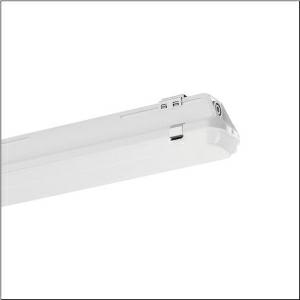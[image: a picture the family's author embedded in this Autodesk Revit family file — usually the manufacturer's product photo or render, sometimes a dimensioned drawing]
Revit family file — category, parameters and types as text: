
# Revit family: monsun_r__12_facade_51ff40mp460h_f970
name_source: partatom
category: Lighting Fixtures
units: mm (PartAtom-declared; Revit-internal decimal feet)

## family parameters
Cut with Voids When Loaded = No
Host = Face
Light Source = No
Part Type = Normal
Room Calculation Point = No
Round Connector Dimension = Use Diameter
Shared = No

## types (1)
- --- (1 x LED, 6110 lm, 33.5 W, 4000K)
    Apparent Load = 34 VA
    CIE Flux Codes = 47 77 93 95 100
    Color Rendering = 80
    Color Temperature = 4000K
    Default Elevation = 1800 mm
    Description = Monsun® 12 facade, damp-proof luminaire, chain hanger, primary optical cover: enclosure, of PMMA, light emission: direct distribution, primary light characteristic: symmetric, installation type: surface-mounted, horizontal mounting, vertical mounting, LED rated luminous flux: 6.110 lm, light colour: 840, colour temperature: 4000K, control gear: ECG, with terminal, 3-pole, max. 2.5mm², mains connection: 220..240V, AC, 50/60Hz, rated input power: 34W, luminaire housing, of glass-fibre reinforced polyester, uncoated, bright grey, length: 1.590 mm, width: 90 mm, height: 88mm, clip for enclosure, of stainless steel (V2A), ceiling mounting element, of stainless steel (V2A), chain hanger, of stainless steel (V2A), protection rating (complete): IP66, insulation class (complete): insulation class I (protective earthing), certification: CE, ENEC, VDE, protection symbol: D, impact resistance: IK06, permissible ambient temperature for indoor applications: -35..+50°C, standard: EN 50419, EN 60598-2-1, exposed outdoor area, packaging unit: 1 piece
    Height = 89 mm
    Lamp = 1 x LED
    Lamp Light Flux = 6110 lm
    Lamp Power = 33.5 W
    Lamp count = 1
    Length = 1590 mm
    Luminous efficacy = 182 lm/W
    Manufacturer = Siteco
    ModVariant = No
    Model = 51FF40MP460H
    Mounting Place = Ceiling
    Mounting Type = Surface mounted
    Number of Poles = 1
    OnlyDefault = Yes
    Power Factor = 1
    Product Name = Monsun® 12 facade
    Product group = damp-proof luminaire | ceiling mounted
    ProductGroupID = 300
    Protection Class = Protection class I
    Protection Degree = IP 66
    RLX_Detail_Level = 1
    RlxData = <blob elided: 89321 chars, md5=7e448a5a>
    Socket = socket
    Standby Power = 0 W
    System Light Flux = 6110 lm
    System Power = 34 W
    Type Comments = factory setting: luminous flux: 100 % | (A | C | E) | 77 mA
    Type Image = l_1004748.jpg
    URL = http://relux.com
    VarID = @adj_135949
    Voltage = 0 V
    Weight = 0.00 kg
    Width = 90 mm

## geometry (parser evidence)
native form markers: Blend x4, Sweep x14
no freeform markers — native parametric forms only
